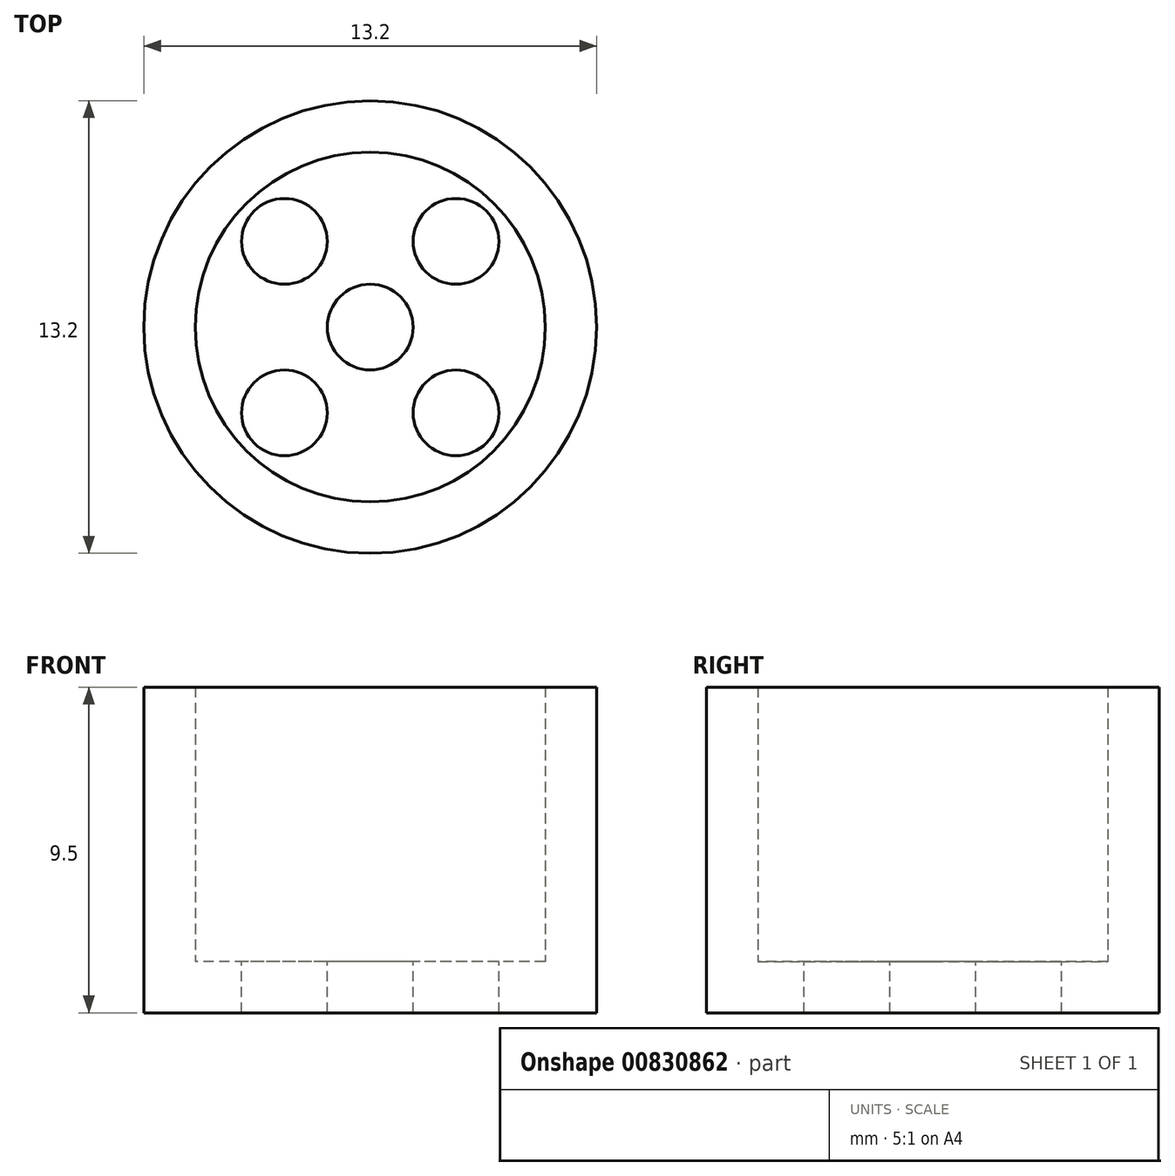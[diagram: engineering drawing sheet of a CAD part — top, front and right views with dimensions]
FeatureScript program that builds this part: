
annotation { "Feature Type Name" : "Feature", "Feature Type Description" : "" }
export const myFeature = defineFeature(function(context is Context, id is Id, definition is map)
    precondition{}
    {
        {
            var Q0;
            Q0=qCreatedBy(makeId("Top.planeOp"),FACE);
            var sketch = newSketch(context, id + "F0", { "sketchPlane" : qUnion([Q0])});
            skCircle(sketch, "E0", {"center": v(0, 0) * mm, "radius": 5.1 * mm});
            skCircle(sketch, "E1", {"center": v(0, 0) * mm, "radius": 6.6 * mm});
            skLineSegment(sketch, "E2.bottom", {"start": v(2.5, 2.5) * mm, "end": v(-2.5, 2.5) * mm, "construction": true});
            skLineSegment(sketch, "E2.top", {"start": v(2.5, -2.5) * mm, "end": v(-2.5, -2.5) * mm, "construction": true});
            skLineSegment(sketch, "E2.left", {"start": v(2.5, 2.5) * mm, "end": v(2.5, -2.5) * mm, "construction": true});
            skLineSegment(sketch, "E2.right", {"start": v(-2.5, 2.5) * mm, "end": v(-2.5, -2.5) * mm, "construction": true});
            skCircle(sketch, "E3", {"center": v(0, 0) * mm, "radius": 1.25 * mm});
            skCircle(sketch, "E4", {"center": v(2.5, 2.5) * mm, "radius": 1.25 * mm});
            skCircle(sketch, "E5", {"center": v(2.5, -2.5) * mm, "radius": 1.25 * mm});
            skCircle(sketch, "E6", {"center": v(-2.5, -2.5) * mm, "radius": 1.25 * mm});
            skCircle(sketch, "E7", {"center": v(-2.5, 2.5) * mm, "radius": 1.25 * mm});
            skSolve(sketch);
        }
        {
            var Q0;
            Q0=makeQuery(id+"F0.imprint","IMPRINT",FACE,{"disambiguationData":[TD([[makeQuery(id+"F0.imprint","IMPRINT",EDGE,{"derivedFrom":sQuery(id+"F0.wireOp",EDGE,"E0")}),1.0]])]});
            var Q1;
            Q1=makeQuery(id+"F0.imprint","IMPRINT",FACE,{"disambiguationData":[TD([[makeQuery(id+"F0.imprint","IMPRINT",EDGE,{"derivedFrom":sQuery(id+"F0.wireOp",EDGE,"E0")}),-1.0]])]});
            extrude(context, id + "F1", {"entities" : qUnion([Q0, Q1]), "oppositeDirection" : true, "depth" : 1.5 * mm, "offsetDistance" : 25 * mm});
        }
        {
            var Q0;
            Q0=makeQuery(id+"F0.imprint","IMPRINT",FACE,{"disambiguationData":[TD([[makeQuery(id+"F0.imprint","IMPRINT",EDGE,{"derivedFrom":sQuery(id+"F0.wireOp",EDGE,"E0")}),-1.0]])]});
            extrude(context, id + "F2", {"entities" : qUnion([Q0]), "operationType" : NewBodyOperationType.ADD, "depth" : 8 * mm, "offsetDistance" : 25 * mm});
        }
    });
